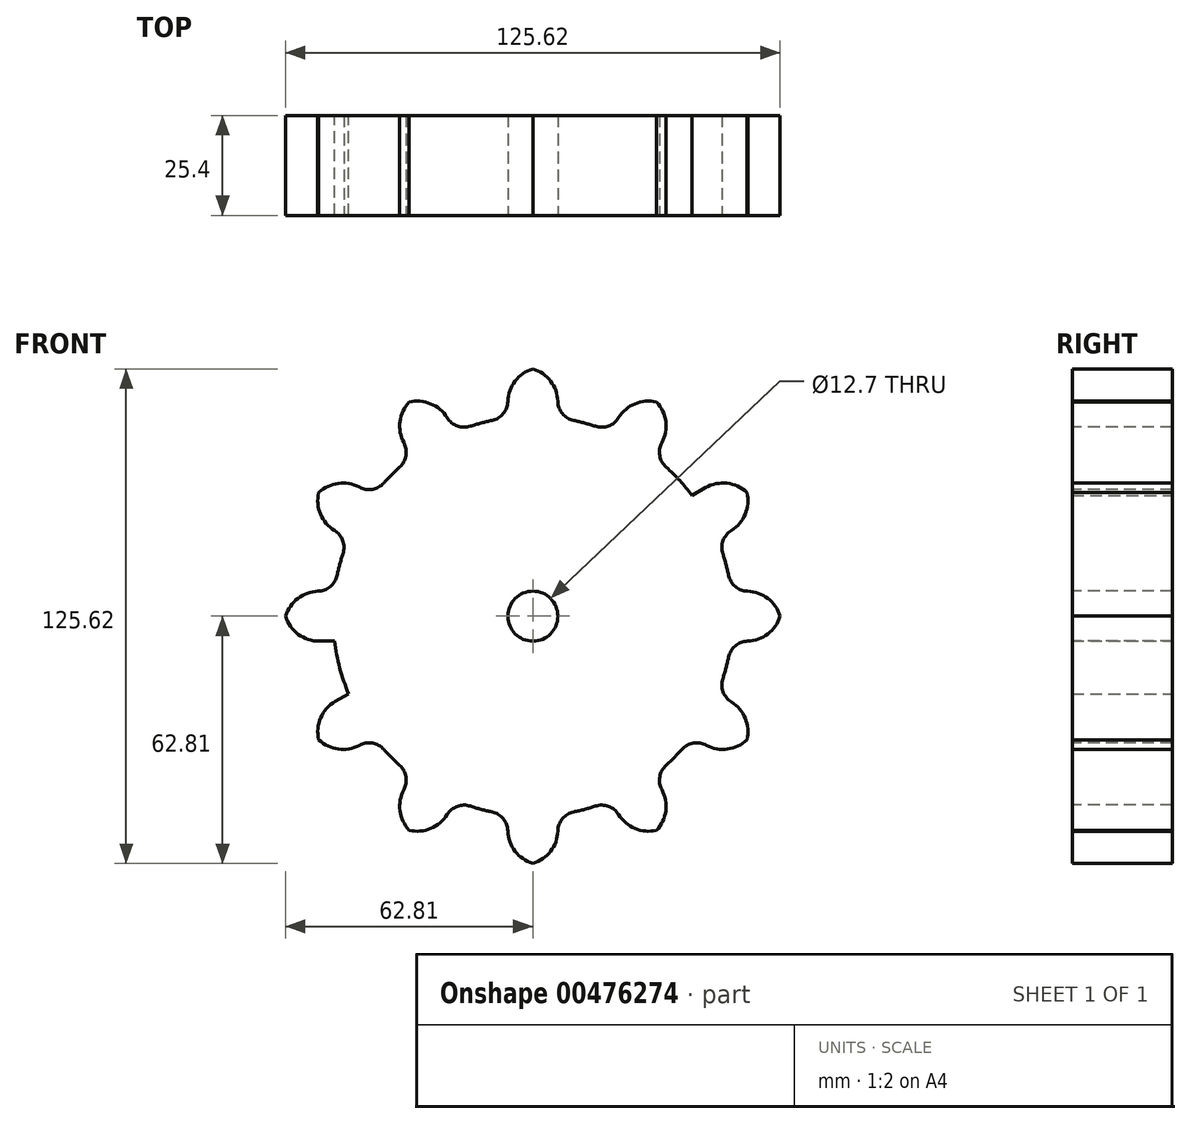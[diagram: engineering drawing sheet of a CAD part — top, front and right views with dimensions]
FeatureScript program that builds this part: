
annotation { "Feature Type Name" : "Feature", "Feature Type Description" : "" }
export const myFeature = defineFeature(function(context is Context, id is Id, definition is map)
    precondition{}
    {
        {
            var Q0;
            Q0=qCreatedBy(makeId("Front.planeOp"),FACE);
            var sketch = newSketch(context, id + "F0", { "sketchPlane" : qUnion([Q0])});
            skCircle(sketch, "E0", {"center": v(0, 0) * mm, "radius": 6.35 * mm});
            skCircle(sketch, "E1", {"center": v(0, 0) * mm, "radius": 50.8 * mm});
            skCircle(sketch, "E2", {"center": v(0, 0) * mm, "radius": 63.5 * mm, "construction": true});
            skLineSegment(sketch, "E3", {"start": v(0, 0) * mm, "end": v(0, 63.5) * mm, "construction": true});
            skLineSegment(sketch, "E4", {"start": v(0, 0) * mm, "end": v(-63.5, 0) * mm, "construction": true});
            skLineSegment(sketch, "E5", {"start": v(0, 0) * mm, "end": v(63.5, 0) * mm, "construction": true});
            skLineSegment(sketch, "E6", {"start": v(0, 0) * mm, "end": v(0, -63.5) * mm, "construction": true});
            skLineSegment(sketch, "E7", {"start": v(31.75, 55) * mm, "end": v(0, 0) * mm, "construction": true});
            skLineSegment(sketch, "E8", {"start": v(0, 0) * mm, "end": v(55, 31.75) * mm, "construction": true});
            skLineSegment(sketch, "E9.bottom", {"start": v(-6.35, -63.18) * mm, "end": v(6.35, -63.18) * mm});
            skLineSegment(sketch, "E9.top", {"start": v(-6.35, 63.18) * mm, "end": v(6.35, 63.18) * mm});
            skLineSegment(sketch, "E9.left", {"start": v(-6.35, -63.18) * mm, "end": v(-6.35, 63.18) * mm});
            skLineSegment(sketch, "E9.right", {"start": v(6.35, -63.18) * mm, "end": v(6.35, 63.18) * mm});
            skLineSegment(sketch, "E10", {"start": v(-37.1, -51.54) * mm, "end": v(26.1, 57.9) * mm});
            skLineSegment(sketch, "E11", {"start": v(-26.1, -57.9) * mm, "end": v(37.1, 51.54) * mm});
            skLineSegment(sketch, "E12", {"start": v(37.1, 51.54) * mm, "end": v(26.1, 57.9) * mm});
            skLineSegment(sketch, "E13", {"start": v(-37.1, -51.54) * mm, "end": v(-26.1, -57.9) * mm});
            skLineSegment(sketch, "E14", {"start": v(-57.9, -26.1) * mm, "end": v(51.54, 37.1) * mm});
            skLineSegment(sketch, "E15", {"start": v(51.54, 37.1) * mm, "end": v(57.9, 26.1) * mm});
            skSolve(sketch);
        }
        {
            var Q0;
            {var subQ5=sQuery(id+"F0.wireOp",EDGE,"E12");Q0=makeQuery(id+"F0.imprint","IMPRINT",FACE,{"disambiguationData":[TD([[makeQuery(id+"F0.imprint","IMPRINT",EDGE,{"derivedFrom":subQ5}),1.0]])]});}
            var Q1;
            {var subQ5=sQuery(id+"F0.wireOp",EDGE,"E9.top");Q1=makeQuery(id+"F0.imprint","IMPRINT",FACE,{"disambiguationData":[TD([[makeQuery(id+"F0.imprint","IMPRINT",EDGE,{"derivedFrom":subQ5}),-1.0]])]});}
            var Q2;
            {var subQ5=sQuery(id+"F0.wireOp",EDGE,"E13");Q2=makeQuery(id+"F0.imprint","IMPRINT",FACE,{"disambiguationData":[TD([[makeQuery(id+"F0.imprint","IMPRINT",EDGE,{"derivedFrom":subQ5}),1.0]])]});}
            var Q3;
            {var subQ5=sQuery(id+"F0.wireOp",EDGE,"E9.bottom");Q3=makeQuery(id+"F0.imprint","IMPRINT",FACE,{"disambiguationData":[TD([[makeQuery(id+"F0.imprint","IMPRINT",EDGE,{"derivedFrom":subQ5}),1.0]])]});}
            var Q4;
            {var subQ0=sQuery(id+"F0.wireOp",EDGE,"E14");var subQ1=sQuery(id+"F0.wireOp",EDGE,"E1");var subQ2=makeQuery(id+"F0.imprint","INTERSECT",VERTEX,{"disambiguationData":[OD(0.0)],"derivedFrom":[subQ1,subQ0]});Q4=makeQuery(id+"F0.imprint","IMPRINT",FACE,{"disambiguationData":[TD([[makeQuery(id+"F0.imprint","IMPRINT",EDGE,{"disambiguationData":[TD([[subQ2,-1.0]])],"derivedFrom":subQ1}),1.0]])]});}
            var Q5;
            {var subQ0=sQuery(id+"F0.wireOp",EDGE,"E10");var subQ1=sQuery(id+"F0.wireOp",EDGE,"E1");var subQ2=makeQuery(id+"F0.imprint","INTERSECT",VERTEX,{"disambiguationData":[OD(0.0)],"derivedFrom":[subQ1,subQ0]});Q5=makeQuery(id+"F0.imprint","IMPRINT",FACE,{"disambiguationData":[TD([[makeQuery(id+"F0.imprint","IMPRINT",EDGE,{"disambiguationData":[TD([[subQ2,-1.0]])],"derivedFrom":subQ1}),1.0]])]});}
            var Q6;
            {var subQ0=sQuery(id+"F0.wireOp",EDGE,"E14");var subQ1=sQuery(id+"F0.wireOp",EDGE,"E1");var subQ2=makeQuery(id+"F0.imprint","INTERSECT",VERTEX,{"disambiguationData":[OD(1.0)],"derivedFrom":[subQ1,subQ0]});Q6=makeQuery(id+"F0.imprint","IMPRINT",FACE,{"disambiguationData":[TD([[makeQuery(id+"F0.imprint","IMPRINT",EDGE,{"disambiguationData":[TD([[subQ2,1.0]])],"derivedFrom":subQ1}),1.0]])]});}
            var Q7;
            {var subQ0=sQuery(id+"F0.wireOp",EDGE,"E11");var subQ1=sQuery(id+"F0.wireOp",EDGE,"E1");var subQ2=makeQuery(id+"F0.imprint","INTERSECT",VERTEX,{"disambiguationData":[OD(1.0)],"derivedFrom":[subQ1,subQ0]});Q7=makeQuery(id+"F0.imprint","IMPRINT",FACE,{"disambiguationData":[TD([[makeQuery(id+"F0.imprint","IMPRINT",EDGE,{"disambiguationData":[TD([[subQ2,-1.0]])],"derivedFrom":subQ1}),1.0]])]});}
            var Q8;
            {var subQ0=sQuery(id+"F0.wireOp",EDGE,"E14");var subQ1=sQuery(id+"F0.wireOp",EDGE,"E1");var subQ2=makeQuery(id+"F0.imprint","INTERSECT",VERTEX,{"disambiguationData":[OD(1.0)],"derivedFrom":[subQ1,subQ0]});Q8=makeQuery(id+"F0.imprint","IMPRINT",FACE,{"disambiguationData":[TD([[makeQuery(id+"F0.imprint","IMPRINT",EDGE,{"disambiguationData":[TD([[subQ2,-1.0]])],"derivedFrom":subQ1}),1.0]])]});}
            var Q9;
            {var subQ0=sQuery(id+"F0.wireOp",EDGE,"E14");var subQ1=sQuery(id+"F0.wireOp",EDGE,"E1");var subQ2=makeQuery(id+"F0.imprint","INTERSECT",VERTEX,{"disambiguationData":[OD(0.0)],"derivedFrom":[subQ1,subQ0]});Q9=makeQuery(id+"F0.imprint","IMPRINT",FACE,{"disambiguationData":[TD([[makeQuery(id+"F0.imprint","IMPRINT",EDGE,{"disambiguationData":[TD([[subQ2,1.0]])],"derivedFrom":subQ1}),1.0]])]});}
            var Q10;
            {var subQ0=sQuery(id+"F0.wireOp",EDGE,"E11");var subQ1=sQuery(id+"F0.wireOp",EDGE,"E1");var subQ2=makeQuery(id+"F0.imprint","INTERSECT",VERTEX,{"disambiguationData":[OD(0.0)],"derivedFrom":[subQ1,subQ0]});Q10=makeQuery(id+"F0.imprint","IMPRINT",FACE,{"disambiguationData":[TD([[makeQuery(id+"F0.imprint","IMPRINT",EDGE,{"disambiguationData":[TD([[subQ2,-1.0]])],"derivedFrom":subQ1}),1.0]])]});}
            var Q11;
            {var subQ1=sQuery(id+"F0.wireOp",EDGE,"E9.right");var subQ5=sQuery(id+"F0.wireOp",EDGE,"E1");var subQ6=makeQuery(id+"F0.imprint","INTERSECT",VERTEX,{"disambiguationData":[OD(0.0)],"derivedFrom":[subQ5,subQ1]});Q11=makeQuery(id+"F0.imprint","IMPRINT",FACE,{"disambiguationData":[TD([[makeQuery(id+"F0.imprint","IMPRINT",EDGE,{"disambiguationData":[TD([[subQ6,-1.0]])],"derivedFrom":subQ5}),1.0]])]});}
            var Q12;
            {var subQ0=sQuery(id+"F0.wireOp",EDGE,"E10");var subQ1=sQuery(id+"F0.wireOp",EDGE,"E1");var subQ2=makeQuery(id+"F0.imprint","INTERSECT",VERTEX,{"disambiguationData":[OD(1.0)],"derivedFrom":[subQ1,subQ0]});Q12=makeQuery(id+"F0.imprint","IMPRINT",FACE,{"disambiguationData":[TD([[makeQuery(id+"F0.imprint","IMPRINT",EDGE,{"disambiguationData":[TD([[subQ2,-1.0]])],"derivedFrom":subQ1}),1.0]])]});}
            var Q13;
            {var subQ2=sQuery(id+"F0.wireOp",EDGE,"E9.left");var subQ4=sQuery(id+"F0.wireOp",EDGE,"E1");var subQ5=makeQuery(id+"F0.imprint","INTERSECT",VERTEX,{"disambiguationData":[OD(1.0)],"derivedFrom":[subQ4,subQ2]});Q13=makeQuery(id+"F0.imprint","IMPRINT",FACE,{"disambiguationData":[TD([[makeQuery(id+"F0.imprint","IMPRINT",EDGE,{"disambiguationData":[TD([[subQ5,-1.0]])],"derivedFrom":subQ4}),1.0]])]});}
            var Q14;
            {var subQ0=sQuery(id+"F0.wireOp",EDGE,"E14");var subQ1=sQuery(id+"F0.wireOp",EDGE,"E9.right");var subQ2=makeQuery(id+"F0.imprint","INTERSECT",VERTEX,{"derivedFrom":[subQ1,subQ0]});Q14=makeQuery(id+"F0.imprint","IMPRINT",FACE,{"disambiguationData":[TD([[makeQuery(id+"F0.imprint","IMPRINT",EDGE,{"disambiguationData":[TD([[subQ2,-1.0]])],"derivedFrom":subQ1}),1.0]])]});}
            var Q15;
            {var subQ0=sQuery(id+"F0.wireOp",EDGE,"E0");var subQ4=makeQuery(id+"F0.imprint","INTERSECT",VERTEX,{"derivedFrom":[subQ0,sQuery(id+"F0.wireOp",EDGE,"E14")]});Q15=makeQuery(id+"F0.imprint","IMPRINT",FACE,{"disambiguationData":[TD([[makeQuery(id+"F0.imprint","IMPRINT",EDGE,{"disambiguationData":[TD([[subQ4,1.0]])],"derivedFrom":subQ0}),1.0]])]});}
            var Q16;
            {var subQ0=sQuery(id+"F0.wireOp",EDGE,"E9.right");var subQ1=makeQuery(id+"F0.imprint","INTERSECT",VERTEX,{"derivedFrom":[sQuery(id+"F0.wireOp",EDGE,"E0"),subQ0]});Q16=makeQuery(id+"F0.imprint","IMPRINT",FACE,{"disambiguationData":[TD([[makeQuery(id+"F0.imprint","IMPRINT",EDGE,{"disambiguationData":[TD([[subQ1,1.0]])],"derivedFrom":subQ0}),-1.0]])]});}
            var Q17;
            {var subQ0=sQuery(id+"F0.wireOp",EDGE,"E14");var subQ1=sQuery(id+"F0.wireOp",EDGE,"E0");var subQ2=makeQuery(id+"F0.imprint","INTERSECT",VERTEX,{"derivedFrom":[subQ1,subQ0]});Q17=makeQuery(id+"F0.imprint","IMPRINT",FACE,{"disambiguationData":[TD([[makeQuery(id+"F0.imprint","IMPRINT",EDGE,{"disambiguationData":[TD([[subQ2,1.0]])],"derivedFrom":subQ1}),-1.0]])]});}
            var Q18;
            {var subQ0=sQuery(id+"F0.wireOp",EDGE,"E9.left");var subQ1=sQuery(id+"F0.wireOp",EDGE,"E0");var subQ2=makeQuery(id+"F0.imprint","INTERSECT",VERTEX,{"derivedFrom":[subQ1,subQ0]});Q18=makeQuery(id+"F0.imprint","IMPRINT",FACE,{"disambiguationData":[TD([[makeQuery(id+"F0.imprint","IMPRINT",EDGE,{"disambiguationData":[TD([[subQ2,-1.0]])],"derivedFrom":subQ1}),-1.0]])]});}
            var Q19;
            {var subQ0=sQuery(id+"F0.wireOp",EDGE,"E10");var subQ1=sQuery(id+"F0.wireOp",EDGE,"E9.left");var subQ2=makeQuery(id+"F0.imprint","INTERSECT",VERTEX,{"derivedFrom":[subQ1,subQ0]});Q19=makeQuery(id+"F0.imprint","IMPRINT",FACE,{"disambiguationData":[TD([[makeQuery(id+"F0.imprint","IMPRINT",EDGE,{"disambiguationData":[TD([[subQ2,-1.0]])],"derivedFrom":subQ1}),-1.0]])]});}
            var Q20;
            {var subQ0=sQuery(id+"F0.wireOp",EDGE,"E9.right");var subQ1=sQuery(id+"F0.wireOp",EDGE,"E0");var subQ2=makeQuery(id+"F0.imprint","INTERSECT",VERTEX,{"derivedFrom":[subQ1,subQ0]});Q20=makeQuery(id+"F0.imprint","IMPRINT",FACE,{"disambiguationData":[TD([[makeQuery(id+"F0.imprint","IMPRINT",EDGE,{"disambiguationData":[TD([[subQ2,1.0]])],"derivedFrom":subQ1}),-1.0]])]});}
            var Q21;
            {var subQ0=sQuery(id+"F0.wireOp",EDGE,"E14");var subQ1=sQuery(id+"F0.wireOp",EDGE,"E0");var subQ2=makeQuery(id+"F0.imprint","INTERSECT",VERTEX,{"derivedFrom":[subQ1,subQ0]});Q21=makeQuery(id+"F0.imprint","IMPRINT",FACE,{"disambiguationData":[TD([[makeQuery(id+"F0.imprint","IMPRINT",EDGE,{"disambiguationData":[TD([[subQ2,-1.0]])],"derivedFrom":subQ1}),-1.0]])]});}
            var Q22;
            {var subQ0=sQuery(id+"F0.wireOp",EDGE,"E10");var subQ1=sQuery(id+"F0.wireOp",EDGE,"E0");var subQ2=makeQuery(id+"F0.imprint","INTERSECT",VERTEX,{"derivedFrom":[subQ1,subQ0]});Q22=makeQuery(id+"F0.imprint","IMPRINT",FACE,{"disambiguationData":[TD([[makeQuery(id+"F0.imprint","IMPRINT",EDGE,{"disambiguationData":[TD([[subQ2,-1.0]])],"derivedFrom":subQ1}),-1.0]])]});}
            extrude(context, id + "F1", {"entities" : qUnion([Q0, Q1, Q2, Q3, Q4, Q5, Q6, Q7, Q8, Q9, Q10, Q11, Q12, Q13, Q14, Q15, Q16, Q17, Q18, Q19, Q20, Q21, Q22]), "depth" : 25.4 * mm});
        }
        {
            var Q0;
            Q0=qCreatedBy(makeId("Front.planeOp"),FACE);
            var sketch = newSketch(context, id + "F2", { "sketchPlane" : qUnion([Q0])});
            skCircle(sketch, "E16", {"center": v(0, 0) * mm, "radius": 6.35 * mm});
            skCircle(sketch, "E17", {"center": v(0, 0) * mm, "radius": 50.8 * mm});
            skCircle(sketch, "E18", {"center": v(0, 0) * mm, "radius": 63.5 * mm, "construction": true});
            skLineSegment(sketch, "E19", {"start": v(0, 0) * mm, "end": v(63.5, 0) * mm, "construction": true});
            skLineSegment(sketch, "E20", {"start": v(0, 0) * mm, "end": v(0, 63.5) * mm, "construction": true});
            skLineSegment(sketch, "E21", {"start": v(0, 0) * mm, "end": v(55, 31.75) * mm, "construction": true});
            skLineSegment(sketch, "E22", {"start": v(-57.9, -26.1) * mm, "end": v(51.54, 37.1) * mm});
            skLineSegment(sketch, "E23", {"start": v(51.54, 37.1) * mm, "end": v(57.9, 26.1) * mm});
            skLineSegment(sketch, "E24", {"start": v(57.9, 26.1) * mm, "end": v(-51.54, -37.1) * mm});
            skLineSegment(sketch, "E25", {"start": v(-51.54, -37.1) * mm, "end": v(-57.9, -26.1) * mm});
            skLineSegment(sketch, "E26.bottom", {"start": v(-63.18, 6.35) * mm, "end": v(63.18, 6.35) * mm});
            skLineSegment(sketch, "E26.top", {"start": v(-63.18, -6.35) * mm, "end": v(63.18, -6.35) * mm});
            skLineSegment(sketch, "E26.left", {"start": v(-63.18, 6.35) * mm, "end": v(-63.18, -6.35) * mm});
            skLineSegment(sketch, "E26.right", {"start": v(63.18, 6.35) * mm, "end": v(63.18, -6.35) * mm});
            skLineSegment(sketch, "E27", {"start": v(-57.9, 26.1) * mm, "end": v(51.54, -37.1) * mm});
            skLineSegment(sketch, "E28", {"start": v(51.54, -37.1) * mm, "end": v(57.9, -26.1) * mm});
            skLineSegment(sketch, "E29", {"start": v(57.9, -26.1) * mm, "end": v(-51.54, 37.1) * mm});
            skLineSegment(sketch, "E30", {"start": v(-51.54, 37.1) * mm, "end": v(-57.9, 26.1) * mm});
            skLineSegment(sketch, "E31", {"start": v(-37.1, 51.54) * mm, "end": v(26.1, -57.9) * mm});
            skLineSegment(sketch, "E32", {"start": v(26.1, -57.9) * mm, "end": v(37.1, -51.54) * mm});
            skLineSegment(sketch, "E33", {"start": v(37.1, -51.54) * mm, "end": v(-26.1, 57.9) * mm});
            skLineSegment(sketch, "E34", {"start": v(-26.1, 57.9) * mm, "end": v(-37.1, 51.54) * mm});
            skSolve(sketch);
        }
        {
            var Q0;
            {var subQ5=sQuery(id+"F2.wireOp",EDGE,"E23");Q0=makeQuery(id+"F2.imprint","IMPRINT",FACE,{"disambiguationData":[TD([[makeQuery(id+"F2.imprint","IMPRINT",EDGE,{"derivedFrom":subQ5}),-1.0]])]});}
            var Q1;
            {var subQ5=sQuery(id+"F2.wireOp",EDGE,"E34");Q1=makeQuery(id+"F2.imprint","IMPRINT",FACE,{"disambiguationData":[TD([[makeQuery(id+"F2.imprint","IMPRINT",EDGE,{"derivedFrom":subQ5}),1.0]])]});}
            var Q2;
            {var subQ5=sQuery(id+"F2.wireOp",EDGE,"E30");Q2=makeQuery(id+"F2.imprint","IMPRINT",FACE,{"disambiguationData":[TD([[makeQuery(id+"F2.imprint","IMPRINT",EDGE,{"derivedFrom":subQ5}),1.0]])]});}
            var Q3;
            {var subQ5=sQuery(id+"F2.wireOp",EDGE,"E26.left");Q3=makeQuery(id+"F2.imprint","IMPRINT",FACE,{"disambiguationData":[TD([[makeQuery(id+"F2.imprint","IMPRINT",EDGE,{"derivedFrom":subQ5}),1.0]])]});}
            var Q4;
            {var subQ5=sQuery(id+"F2.wireOp",EDGE,"E25");Q4=makeQuery(id+"F2.imprint","IMPRINT",FACE,{"disambiguationData":[TD([[makeQuery(id+"F2.imprint","IMPRINT",EDGE,{"derivedFrom":subQ5}),-1.0]])]});}
            var Q5;
            {var subQ5=sQuery(id+"F2.wireOp",EDGE,"E32");Q5=makeQuery(id+"F2.imprint","IMPRINT",FACE,{"disambiguationData":[TD([[makeQuery(id+"F2.imprint","IMPRINT",EDGE,{"derivedFrom":subQ5}),1.0]])]});}
            var Q6;
            {var subQ5=sQuery(id+"F2.wireOp",EDGE,"E28");Q6=makeQuery(id+"F2.imprint","IMPRINT",FACE,{"disambiguationData":[TD([[makeQuery(id+"F2.imprint","IMPRINT",EDGE,{"derivedFrom":subQ5}),1.0]])]});}
            var Q7;
            {var subQ5=sQuery(id+"F2.wireOp",EDGE,"E26.right");Q7=makeQuery(id+"F2.imprint","IMPRINT",FACE,{"disambiguationData":[TD([[makeQuery(id+"F2.imprint","IMPRINT",EDGE,{"derivedFrom":subQ5}),-1.0]])]});}
            var Q8;
            {var subQ0=sQuery(id+"F2.wireOp",EDGE,"E24");var subQ1=sQuery(id+"F2.wireOp",EDGE,"E17");var subQ2=makeQuery(id+"F2.imprint","INTERSECT",VERTEX,{"disambiguationData":[OD(0.0)],"derivedFrom":[subQ1,subQ0]});Q8=makeQuery(id+"F2.imprint","IMPRINT",FACE,{"disambiguationData":[TD([[makeQuery(id+"F2.imprint","IMPRINT",EDGE,{"disambiguationData":[TD([[subQ2,1.0]])],"derivedFrom":subQ1}),1.0]])]});}
            var Q9;
            {var subQ0=sQuery(id+"F2.wireOp",EDGE,"E22");var subQ1=sQuery(id+"F2.wireOp",EDGE,"E17");var subQ2=makeQuery(id+"F2.imprint","INTERSECT",VERTEX,{"disambiguationData":[OD(0.0)],"derivedFrom":[subQ1,subQ0]});Q9=makeQuery(id+"F2.imprint","IMPRINT",FACE,{"disambiguationData":[TD([[makeQuery(id+"F2.imprint","IMPRINT",EDGE,{"disambiguationData":[TD([[subQ2,-1.0]])],"derivedFrom":subQ1}),1.0]])]});}
            var Q10;
            {var subQ0=sQuery(id+"F2.wireOp",EDGE,"E31");var subQ1=sQuery(id+"F2.wireOp",EDGE,"E17");var subQ2=makeQuery(id+"F2.imprint","INTERSECT",VERTEX,{"disambiguationData":[OD(0.0)],"derivedFrom":[subQ1,subQ0]});Q10=makeQuery(id+"F2.imprint","IMPRINT",FACE,{"disambiguationData":[TD([[makeQuery(id+"F2.imprint","IMPRINT",EDGE,{"disambiguationData":[TD([[subQ2,-1.0]])],"derivedFrom":subQ1}),1.0]])]});}
            var Q11;
            {var subQ0=sQuery(id+"F2.wireOp",EDGE,"E27");var subQ1=sQuery(id+"F2.wireOp",EDGE,"E17");var subQ2=makeQuery(id+"F2.imprint","INTERSECT",VERTEX,{"disambiguationData":[OD(0.0)],"derivedFrom":[subQ1,subQ0]});Q11=makeQuery(id+"F2.imprint","IMPRINT",FACE,{"disambiguationData":[TD([[makeQuery(id+"F2.imprint","IMPRINT",EDGE,{"disambiguationData":[TD([[subQ2,-1.0]])],"derivedFrom":subQ1}),1.0]])]});}
            var Q12;
            {var subQ0=sQuery(id+"F2.wireOp",EDGE,"E26.top");var subQ1=sQuery(id+"F2.wireOp",EDGE,"E17");var subQ2=makeQuery(id+"F2.imprint","INTERSECT",VERTEX,{"disambiguationData":[OD(0.0)],"derivedFrom":[subQ1,subQ0]});Q12=makeQuery(id+"F2.imprint","IMPRINT",FACE,{"disambiguationData":[TD([[makeQuery(id+"F2.imprint","IMPRINT",EDGE,{"disambiguationData":[TD([[subQ2,-1.0]])],"derivedFrom":subQ1}),1.0]])]});}
            var Q13;
            {var subQ0=sQuery(id+"F2.wireOp",EDGE,"E24");var subQ1=sQuery(id+"F2.wireOp",EDGE,"E17");var subQ2=makeQuery(id+"F2.imprint","INTERSECT",VERTEX,{"disambiguationData":[OD(1.0)],"derivedFrom":[subQ1,subQ0]});Q13=makeQuery(id+"F2.imprint","IMPRINT",FACE,{"disambiguationData":[TD([[makeQuery(id+"F2.imprint","IMPRINT",EDGE,{"disambiguationData":[TD([[subQ2,-1.0]])],"derivedFrom":subQ1}),1.0]])]});}
            var Q14;
            {var subQ0=sQuery(id+"F2.wireOp",EDGE,"E33");var subQ1=sQuery(id+"F2.wireOp",EDGE,"E17");var subQ2=makeQuery(id+"F2.imprint","INTERSECT",VERTEX,{"disambiguationData":[OD(1.0)],"derivedFrom":[subQ1,subQ0]});Q14=makeQuery(id+"F2.imprint","IMPRINT",FACE,{"disambiguationData":[TD([[makeQuery(id+"F2.imprint","IMPRINT",EDGE,{"disambiguationData":[TD([[subQ2,-1.0]])],"derivedFrom":subQ1}),1.0]])]});}
            var Q15;
            {var subQ0=sQuery(id+"F2.wireOp",EDGE,"E29");var subQ1=sQuery(id+"F2.wireOp",EDGE,"E17");var subQ2=makeQuery(id+"F2.imprint","INTERSECT",VERTEX,{"disambiguationData":[OD(1.0)],"derivedFrom":[subQ1,subQ0]});Q15=makeQuery(id+"F2.imprint","IMPRINT",FACE,{"disambiguationData":[TD([[makeQuery(id+"F2.imprint","IMPRINT",EDGE,{"disambiguationData":[TD([[subQ2,-1.0]])],"derivedFrom":subQ1}),1.0]])]});}
            var Q16;
            {var subQ1=sQuery(id+"F2.wireOp",EDGE,"E24");var subQ5=sQuery(id+"F2.wireOp",EDGE,"E17");var subQ6=makeQuery(id+"F2.imprint","INTERSECT",VERTEX,{"disambiguationData":[OD(0.0)],"derivedFrom":[subQ5,subQ1]});Q16=makeQuery(id+"F2.imprint","IMPRINT",FACE,{"disambiguationData":[TD([[makeQuery(id+"F2.imprint","IMPRINT",EDGE,{"disambiguationData":[TD([[subQ6,-1.0]])],"derivedFrom":subQ5}),1.0]])]});}
            var Q17;
            {var subQ1=sQuery(id+"F2.wireOp",EDGE,"E17");var subQ7=sQuery(id+"F2.wireOp",EDGE,"E33");var subQ9=makeQuery(id+"F2.imprint","INTERSECT",VERTEX,{"disambiguationData":[OD(0.0)],"derivedFrom":[subQ1,subQ7]});Q17=makeQuery(id+"F2.imprint","IMPRINT",FACE,{"disambiguationData":[TD([[makeQuery(id+"F2.imprint","IMPRINT",EDGE,{"disambiguationData":[TD([[subQ9,-1.0]])],"derivedFrom":subQ1}),1.0]])]});}
            var Q18;
            {var subQ0=sQuery(id+"F2.wireOp",EDGE,"E29");var subQ1=sQuery(id+"F2.wireOp",EDGE,"E17");var subQ2=makeQuery(id+"F2.imprint","INTERSECT",VERTEX,{"disambiguationData":[OD(0.0)],"derivedFrom":[subQ1,subQ0]});Q18=makeQuery(id+"F2.imprint","IMPRINT",FACE,{"disambiguationData":[TD([[makeQuery(id+"F2.imprint","IMPRINT",EDGE,{"disambiguationData":[TD([[subQ2,-1.0]])],"derivedFrom":subQ1}),1.0]])]});}
            var Q19;
            {var subQ1=sQuery(id+"F2.wireOp",EDGE,"E17");var subQ5=sQuery(id+"F2.wireOp",EDGE,"E26.bottom");var subQ6=makeQuery(id+"F2.imprint","INTERSECT",VERTEX,{"disambiguationData":[OD(1.0)],"derivedFrom":[subQ1,subQ5]});Q19=makeQuery(id+"F2.imprint","IMPRINT",FACE,{"disambiguationData":[TD([[makeQuery(id+"F2.imprint","IMPRINT",EDGE,{"disambiguationData":[TD([[subQ6,-1.0]])],"derivedFrom":subQ1}),1.0]])]});}
            var Q20;
            {var subQ1=sQuery(id+"F2.wireOp",EDGE,"E22");var subQ5=sQuery(id+"F2.wireOp",EDGE,"E17");var subQ6=makeQuery(id+"F2.imprint","INTERSECT",VERTEX,{"disambiguationData":[OD(1.0)],"derivedFrom":[subQ5,subQ1]});Q20=makeQuery(id+"F2.imprint","IMPRINT",FACE,{"disambiguationData":[TD([[makeQuery(id+"F2.imprint","IMPRINT",EDGE,{"disambiguationData":[TD([[subQ6,-1.0]])],"derivedFrom":subQ5}),1.0]])]});}
            var Q21;
            {var subQ0=sQuery(id+"F2.wireOp",EDGE,"E31");var subQ1=sQuery(id+"F2.wireOp",EDGE,"E17");var subQ2=makeQuery(id+"F2.imprint","INTERSECT",VERTEX,{"disambiguationData":[OD(1.0)],"derivedFrom":[subQ1,subQ0]});Q21=makeQuery(id+"F2.imprint","IMPRINT",FACE,{"disambiguationData":[TD([[makeQuery(id+"F2.imprint","IMPRINT",EDGE,{"disambiguationData":[TD([[subQ2,-1.0]])],"derivedFrom":subQ1}),1.0]])]});}
            var Q22;
            {var subQ1=sQuery(id+"F2.wireOp",EDGE,"E17");var subQ7=sQuery(id+"F2.wireOp",EDGE,"E27");var subQ8=makeQuery(id+"F2.imprint","INTERSECT",VERTEX,{"disambiguationData":[OD(1.0)],"derivedFrom":[subQ1,subQ7]});Q22=makeQuery(id+"F2.imprint","IMPRINT",FACE,{"disambiguationData":[TD([[makeQuery(id+"F2.imprint","IMPRINT",EDGE,{"disambiguationData":[TD([[subQ8,-1.0]])],"derivedFrom":subQ1}),1.0]])]});}
            var Q23;
            {var subQ1=sQuery(id+"F2.wireOp",EDGE,"E17");var subQ5=sQuery(id+"F2.wireOp",EDGE,"E26.bottom");var subQ6=makeQuery(id+"F2.imprint","INTERSECT",VERTEX,{"disambiguationData":[OD(0.0)],"derivedFrom":[subQ1,subQ5]});Q23=makeQuery(id+"F2.imprint","IMPRINT",FACE,{"disambiguationData":[TD([[makeQuery(id+"F2.imprint","IMPRINT",EDGE,{"disambiguationData":[TD([[subQ6,1.0]])],"derivedFrom":subQ1}),1.0]])]});}
            var Q24;
            {var subQ0=sQuery(id+"F2.wireOp",EDGE,"E27");var subQ1=sQuery(id+"F2.wireOp",EDGE,"E22");var subQ2=makeQuery(id+"F2.imprint","INTERSECT",VERTEX,{"derivedFrom":[subQ1,subQ0]});Q24=makeQuery(id+"F2.imprint","IMPRINT",FACE,{"disambiguationData":[TD([[makeQuery(id+"F2.imprint","IMPRINT",EDGE,{"disambiguationData":[TD([[subQ2,-1.0]])],"derivedFrom":subQ1}),1.0]])]});}
            var Q25;
            {var subQ0=sQuery(id+"F2.wireOp",EDGE,"E22");var subQ1=sQuery(id+"F2.wireOp",EDGE,"E16");var subQ2=makeQuery(id+"F2.imprint","INTERSECT",VERTEX,{"derivedFrom":[subQ1,subQ0]});Q25=makeQuery(id+"F2.imprint","IMPRINT",FACE,{"disambiguationData":[TD([[makeQuery(id+"F2.imprint","IMPRINT",EDGE,{"disambiguationData":[TD([[subQ2,-1.0]])],"derivedFrom":subQ1}),-1.0]])]});}
            var Q26;
            {var subQ0=sQuery(id+"F2.wireOp",EDGE,"E26.bottom");var subQ1=sQuery(id+"F2.wireOp",EDGE,"E24");var subQ2=makeQuery(id+"F2.imprint","INTERSECT",VERTEX,{"derivedFrom":[subQ1,subQ0]});Q26=makeQuery(id+"F2.imprint","IMPRINT",FACE,{"disambiguationData":[TD([[makeQuery(id+"F2.imprint","IMPRINT",EDGE,{"disambiguationData":[TD([[subQ2,-1.0]])],"derivedFrom":subQ1}),-1.0]])]});}
            var Q27;
            {var subQ0=sQuery(id+"F2.wireOp",EDGE,"E24");var subQ1=makeQuery(id+"F2.imprint","INTERSECT",VERTEX,{"derivedFrom":[sQuery(id+"F2.wireOp",EDGE,"E16"),subQ0]});Q27=makeQuery(id+"F2.imprint","IMPRINT",FACE,{"disambiguationData":[TD([[makeQuery(id+"F2.imprint","IMPRINT",EDGE,{"disambiguationData":[TD([[subQ1,1.0]])],"derivedFrom":subQ0}),1.0]])]});}
            var Q28;
            {var subQ0=sQuery(id+"F2.wireOp",EDGE,"E26.top");var subQ1=sQuery(id+"F2.wireOp",EDGE,"E22");var subQ2=makeQuery(id+"F2.imprint","INTERSECT",VERTEX,{"derivedFrom":[subQ1,subQ0]});Q28=makeQuery(id+"F2.imprint","IMPRINT",FACE,{"disambiguationData":[TD([[makeQuery(id+"F2.imprint","IMPRINT",EDGE,{"disambiguationData":[TD([[subQ2,-1.0]])],"derivedFrom":subQ1}),-1.0]])]});}
            var Q29;
            {var subQ0=sQuery(id+"F2.wireOp",EDGE,"E26.bottom");var subQ1=sQuery(id+"F2.wireOp",EDGE,"E22");var subQ2=makeQuery(id+"F2.imprint","INTERSECT",VERTEX,{"derivedFrom":[subQ1,subQ0]});Q29=makeQuery(id+"F2.imprint","IMPRINT",FACE,{"disambiguationData":[TD([[makeQuery(id+"F2.imprint","IMPRINT",EDGE,{"disambiguationData":[TD([[subQ2,-1.0]])],"derivedFrom":subQ1}),1.0]])]});}
            var Q30;
            {var subQ0=sQuery(id+"F2.wireOp",EDGE,"E27");var subQ1=sQuery(id+"F2.wireOp",EDGE,"E22");var subQ2=makeQuery(id+"F2.imprint","INTERSECT",VERTEX,{"derivedFrom":[subQ1,subQ0]});Q30=makeQuery(id+"F2.imprint","IMPRINT",FACE,{"disambiguationData":[TD([[makeQuery(id+"F2.imprint","IMPRINT",EDGE,{"disambiguationData":[TD([[subQ2,-1.0]])],"derivedFrom":subQ1}),-1.0]])]});}
            var Q31;
            {var subQ0=sQuery(id+"F2.wireOp",EDGE,"E26.top");var subQ1=sQuery(id+"F2.wireOp",EDGE,"E24");var subQ2=makeQuery(id+"F2.imprint","INTERSECT",VERTEX,{"derivedFrom":[subQ1,subQ0]});Q31=makeQuery(id+"F2.imprint","IMPRINT",FACE,{"disambiguationData":[TD([[makeQuery(id+"F2.imprint","IMPRINT",EDGE,{"disambiguationData":[TD([[subQ2,-1.0]])],"derivedFrom":subQ1}),1.0]])]});}
            var Q32;
            {var subQ0=sQuery(id+"F2.wireOp",EDGE,"E29");var subQ1=sQuery(id+"F2.wireOp",EDGE,"E24");var subQ2=makeQuery(id+"F2.imprint","INTERSECT",VERTEX,{"derivedFrom":[subQ1,subQ0]});Q32=makeQuery(id+"F2.imprint","IMPRINT",FACE,{"disambiguationData":[TD([[makeQuery(id+"F2.imprint","IMPRINT",EDGE,{"disambiguationData":[TD([[subQ2,-1.0]])],"derivedFrom":subQ1}),-1.0]])]});}
            var Q33;
            {var subQ0=sQuery(id+"F2.wireOp",EDGE,"E27");var subQ1=sQuery(id+"F2.wireOp",EDGE,"E24");var subQ2=makeQuery(id+"F2.imprint","INTERSECT",VERTEX,{"derivedFrom":[subQ1,subQ0]});Q33=makeQuery(id+"F2.imprint","IMPRINT",FACE,{"disambiguationData":[TD([[makeQuery(id+"F2.imprint","IMPRINT",EDGE,{"disambiguationData":[TD([[subQ2,-1.0]])],"derivedFrom":subQ1}),-1.0]])]});}
            var Q34;
            {var subQ0=sQuery(id+"F2.wireOp",EDGE,"E33");var subQ1=sQuery(id+"F2.wireOp",EDGE,"E16");var subQ2=makeQuery(id+"F2.imprint","INTERSECT",VERTEX,{"derivedFrom":[subQ1,subQ0]});Q34=makeQuery(id+"F2.imprint","IMPRINT",FACE,{"disambiguationData":[TD([[makeQuery(id+"F2.imprint","IMPRINT",EDGE,{"disambiguationData":[TD([[subQ2,1.0]])],"derivedFrom":subQ1}),-1.0]])]});}
            var Q35;
            {var subQ0=sQuery(id+"F2.wireOp",EDGE,"E22");var subQ1=makeQuery(id+"F2.imprint","INTERSECT",VERTEX,{"derivedFrom":[sQuery(id+"F2.wireOp",EDGE,"E16"),subQ0]});Q35=makeQuery(id+"F2.imprint","IMPRINT",FACE,{"disambiguationData":[TD([[makeQuery(id+"F2.imprint","IMPRINT",EDGE,{"disambiguationData":[TD([[subQ1,1.0]])],"derivedFrom":subQ0}),1.0]])]});}
            var Q36;
            {var subQ0=sQuery(id+"F2.wireOp",EDGE,"E29");var subQ1=sQuery(id+"F2.wireOp",EDGE,"E24");var subQ2=makeQuery(id+"F2.imprint","INTERSECT",VERTEX,{"derivedFrom":[subQ1,subQ0]});Q36=makeQuery(id+"F2.imprint","IMPRINT",FACE,{"disambiguationData":[TD([[makeQuery(id+"F2.imprint","IMPRINT",EDGE,{"disambiguationData":[TD([[subQ2,-1.0]])],"derivedFrom":subQ1}),1.0]])]});}
            var Q37;
            {var subQ0=sQuery(id+"F2.wireOp",EDGE,"E26.top");var subQ1=sQuery(id+"F2.wireOp",EDGE,"E24");var subQ2=makeQuery(id+"F2.imprint","INTERSECT",VERTEX,{"derivedFrom":[subQ1,subQ0]});Q37=makeQuery(id+"F2.imprint","IMPRINT",FACE,{"disambiguationData":[TD([[makeQuery(id+"F2.imprint","IMPRINT",EDGE,{"disambiguationData":[TD([[subQ2,-1.0]])],"derivedFrom":subQ1}),-1.0]])]});}
            var Q38;
            {var subQ0=sQuery(id+"F2.wireOp",EDGE,"E29");var subQ1=sQuery(id+"F2.wireOp",EDGE,"E26.bottom");var subQ2=makeQuery(id+"F2.imprint","INTERSECT",VERTEX,{"derivedFrom":[subQ1,subQ0]});Q38=makeQuery(id+"F2.imprint","IMPRINT",FACE,{"disambiguationData":[TD([[makeQuery(id+"F2.imprint","IMPRINT",EDGE,{"disambiguationData":[TD([[subQ2,-1.0]])],"derivedFrom":subQ1}),-1.0]])]});}
            var Q39;
            {var subQ0=sQuery(id+"F2.wireOp",EDGE,"E29");var subQ1=sQuery(id+"F2.wireOp",EDGE,"E22");var subQ2=makeQuery(id+"F2.imprint","INTERSECT",VERTEX,{"derivedFrom":[subQ1,subQ0]});Q39=makeQuery(id+"F2.imprint","IMPRINT",FACE,{"disambiguationData":[TD([[makeQuery(id+"F2.imprint","IMPRINT",EDGE,{"disambiguationData":[TD([[subQ2,-1.0]])],"derivedFrom":subQ1}),-1.0]])]});}
            var Q40;
            {var subQ0=sQuery(id+"F2.wireOp",EDGE,"E31");var subQ1=sQuery(id+"F2.wireOp",EDGE,"E26.top");var subQ2=makeQuery(id+"F2.imprint","INTERSECT",VERTEX,{"derivedFrom":[subQ1,subQ0]});Q40=makeQuery(id+"F2.imprint","IMPRINT",FACE,{"disambiguationData":[TD([[makeQuery(id+"F2.imprint","IMPRINT",EDGE,{"disambiguationData":[TD([[subQ2,-1.0]])],"derivedFrom":subQ1}),1.0]])]});}
            var Q41;
            {var subQ0=sQuery(id+"F2.wireOp",EDGE,"E16");var subQ4=makeQuery(id+"F2.imprint","INTERSECT",VERTEX,{"derivedFrom":[subQ0,sQuery(id+"F2.wireOp",EDGE,"E29")]});Q41=makeQuery(id+"F2.imprint","IMPRINT",FACE,{"disambiguationData":[TD([[makeQuery(id+"F2.imprint","IMPRINT",EDGE,{"disambiguationData":[TD([[subQ4,1.0]])],"derivedFrom":subQ0}),1.0]])]});}
            var Q42;
            {var subQ0=sQuery(id+"F2.wireOp",EDGE,"E26.bottom");var subQ1=sQuery(id+"F2.wireOp",EDGE,"E16");var subQ2=makeQuery(id+"F2.imprint","INTERSECT",VERTEX,{"derivedFrom":[subQ1,subQ0]});Q42=makeQuery(id+"F2.imprint","IMPRINT",FACE,{"disambiguationData":[TD([[makeQuery(id+"F2.imprint","IMPRINT",EDGE,{"disambiguationData":[TD([[subQ2,-1.0]])],"derivedFrom":subQ1}),-1.0]])]});}
            var Q43;
            {var subQ0=sQuery(id+"F2.wireOp",EDGE,"E26.top");var subQ1=sQuery(id+"F2.wireOp",EDGE,"E16");var subQ2=makeQuery(id+"F2.imprint","INTERSECT",VERTEX,{"derivedFrom":[subQ1,subQ0]});Q43=makeQuery(id+"F2.imprint","IMPRINT",FACE,{"disambiguationData":[TD([[makeQuery(id+"F2.imprint","IMPRINT",EDGE,{"disambiguationData":[TD([[subQ2,-1.0]])],"derivedFrom":subQ1}),-1.0]])]});}
            var Q44;
            {var subQ0=sQuery(id+"F2.wireOp",EDGE,"E26.bottom");var subQ1=sQuery(id+"F2.wireOp",EDGE,"E22");var subQ2=makeQuery(id+"F2.imprint","INTERSECT",VERTEX,{"derivedFrom":[subQ1,subQ0]});Q44=makeQuery(id+"F2.imprint","IMPRINT",FACE,{"disambiguationData":[TD([[makeQuery(id+"F2.imprint","IMPRINT",EDGE,{"disambiguationData":[TD([[subQ2,-1.0]])],"derivedFrom":subQ1}),-1.0]])]});}
            var Q45;
            {var subQ0=sQuery(id+"F2.wireOp",EDGE,"E29");var subQ1=sQuery(id+"F2.wireOp",EDGE,"E16");var subQ2=makeQuery(id+"F2.imprint","INTERSECT",VERTEX,{"derivedFrom":[subQ1,subQ0]});Q45=makeQuery(id+"F2.imprint","IMPRINT",FACE,{"disambiguationData":[TD([[makeQuery(id+"F2.imprint","IMPRINT",EDGE,{"disambiguationData":[TD([[subQ2,-1.0]])],"derivedFrom":subQ1}),-1.0]])]});}
            var Q46;
            {var subQ0=sQuery(id+"F2.wireOp",EDGE,"E27");var subQ1=sQuery(id+"F2.wireOp",EDGE,"E16");var subQ2=makeQuery(id+"F2.imprint","INTERSECT",VERTEX,{"derivedFrom":[subQ1,subQ0]});Q46=makeQuery(id+"F2.imprint","IMPRINT",FACE,{"disambiguationData":[TD([[makeQuery(id+"F2.imprint","IMPRINT",EDGE,{"disambiguationData":[TD([[subQ2,-1.0]])],"derivedFrom":subQ1}),-1.0]])]});}
            var Q47;
            {var subQ0=sQuery(id+"F2.wireOp",EDGE,"E31");var subQ1=sQuery(id+"F2.wireOp",EDGE,"E16");var subQ2=makeQuery(id+"F2.imprint","INTERSECT",VERTEX,{"derivedFrom":[subQ1,subQ0]});Q47=makeQuery(id+"F2.imprint","IMPRINT",FACE,{"disambiguationData":[TD([[makeQuery(id+"F2.imprint","IMPRINT",EDGE,{"disambiguationData":[TD([[subQ2,-1.0]])],"derivedFrom":subQ1}),-1.0]])]});}
            var Q48;
            {var subQ0=sQuery(id+"F2.wireOp",EDGE,"E29");var subQ1=sQuery(id+"F2.wireOp",EDGE,"E16");var subQ2=makeQuery(id+"F2.imprint","INTERSECT",VERTEX,{"derivedFrom":[subQ1,subQ0]});Q48=makeQuery(id+"F2.imprint","IMPRINT",FACE,{"disambiguationData":[TD([[makeQuery(id+"F2.imprint","IMPRINT",EDGE,{"disambiguationData":[TD([[subQ2,1.0]])],"derivedFrom":subQ1}),-1.0]])]});}
            extrude(context, id + "F3", {"entities" : qUnion([Q0, Q1, Q2, Q3, Q4, Q5, Q6, Q7, Q8, Q9, Q10, Q11, Q12, Q13, Q14, Q15, Q16, Q17, Q18, Q19, Q20, Q21, Q22, Q23, Q24, Q25, Q26, Q27, Q28, Q29, Q30, Q31, Q32, Q33, Q34, Q35, Q36, Q37, Q38, Q39, Q40, Q41, Q42, Q43, Q44, Q45, Q46, Q47, Q48]), "operationType" : NewBodyOperationType.ADD, "depth" : 25.4 * mm});
        }
        {
            var Q0;
            Q0=makeQuery(id+"F3.boolean.opBoolean","MERGE",FACE,{"derivedFrom":[makeQuery(id+"F1.opExtrude","CAP_FACE",FACE,{"disambiguationData":[OSD([sQuery(id+"F0.wireOp",EDGE,"E1"),sQuery(id+"F0.wireOp",EDGE,"E9.bottom"),sQuery(id+"F0.wireOp",EDGE,"E9.top"),sQuery(id+"F0.wireOp",EDGE,"E9.left"),sQuery(id+"F0.wireOp",EDGE,"E9.right"),sQuery(id+"F0.wireOp",EDGE,"E10"),sQuery(id+"F0.wireOp",EDGE,"E11"),sQuery(id+"F0.wireOp",EDGE,"E12"),sQuery(id+"F0.wireOp",EDGE,"E13")])],"isStart":false}),makeQuery(id+"F3.opExtrude","CAP_FACE",FACE,{"disambiguationData":[OSD([sQuery(id+"F2.wireOp",EDGE,"E17"),sQuery(id+"F2.wireOp",EDGE,"E22"),sQuery(id+"F2.wireOp",EDGE,"E23"),sQuery(id+"F2.wireOp",EDGE,"E24"),sQuery(id+"F2.wireOp",EDGE,"E25"),sQuery(id+"F2.wireOp",EDGE,"E26.bottom"),sQuery(id+"F2.wireOp",EDGE,"E26.top"),sQuery(id+"F2.wireOp",EDGE,"E26.left"),sQuery(id+"F2.wireOp",EDGE,"E26.right"),sQuery(id+"F2.wireOp",EDGE,"E27"),sQuery(id+"F2.wireOp",EDGE,"E28"),sQuery(id+"F2.wireOp",EDGE,"E29"),sQuery(id+"F2.wireOp",EDGE,"E30"),sQuery(id+"F2.wireOp",EDGE,"E31"),sQuery(id+"F2.wireOp",EDGE,"E32"),sQuery(id+"F2.wireOp",EDGE,"E33"),sQuery(id+"F2.wireOp",EDGE,"E34")])],"isStart":false})]});
            var sketch = newSketch(context, id + "F4", { "sketchPlane" : qUnion([Q0])});
            skCircle(sketch, "E35", {"center": v(0, 0) * mm, "radius": 6.35 * mm});
            skSolve(sketch);
        }
        {
            var Q0;
            Q0=makeQuery(id+"F4.imprint","IMPRINT",FACE,{"disambiguationData":[TD([[makeQuery(id+"F4.imprint","IMPRINT",EDGE,{"derivedFrom":sQuery(id+"F4.wireOp",EDGE,"gMkGZPPQ-I52G-XJL4-xDoI-vPj4hhmsiVuW")}),1.0]])]});
            var Q1;
            Q1=makeQuery(id+"F4.imprint","IMPRINT",FACE,{"disambiguationData":[TD([[makeQuery(id+"F4.imprint","IMPRINT",EDGE,{"derivedFrom":sQuery(id+"F4.wireOp",EDGE,"E35")}),1.0]])]});
            extrude(context, id + "F5", {"entities" : qUnion([Q0, Q1]), "operationType" : NewBodyOperationType.REMOVE, "oppositeDirection" : true, "depth" : 25.4 * mm});
        }
        {
            var Q0;
            Q0=makeQuery(id+"F1.opExtrude","SWEPT_EDGE",EDGE,{"disambiguationData":[OSD([sQuery(id+"F0.wireOp",EDGE,"E9.top"),sQuery(id+"F0.wireOp",EDGE,"E9.left")])]});
            var Q1;
            Q1=makeQuery(id+"F1.opExtrude","SWEPT_EDGE",EDGE,{"disambiguationData":[OSD([sQuery(id+"F0.wireOp",EDGE,"E9.top"),sQuery(id+"F0.wireOp",EDGE,"E9.right")])]});
            var Q2;
            Q2=makeQuery(id+"F1.opExtrude","SWEPT_EDGE",EDGE,{"disambiguationData":[OSD([sQuery(id+"F0.wireOp",EDGE,"E10"),sQuery(id+"F0.wireOp",EDGE,"E12")])]});
            var Q3;
            Q3=makeQuery(id+"F1.opExtrude","SWEPT_EDGE",EDGE,{"disambiguationData":[OSD([sQuery(id+"F0.wireOp",EDGE,"E11"),sQuery(id+"F0.wireOp",EDGE,"E12")])]});
            var Q4;
            Q4=makeQuery(id+"F3.opExtrude","SWEPT_EDGE",EDGE,{"disambiguationData":[OSD([sQuery(id+"F2.wireOp",EDGE,"E22"),sQuery(id+"F2.wireOp",EDGE,"E23")])]});
            var Q5;
            Q5=makeQuery(id+"F3.opExtrude","SWEPT_EDGE",EDGE,{"disambiguationData":[OSD([sQuery(id+"F2.wireOp",EDGE,"E23"),sQuery(id+"F2.wireOp",EDGE,"E24")])]});
            var Q6;
            Q6=makeQuery(id+"F3.opExtrude","SWEPT_EDGE",EDGE,{"disambiguationData":[OSD([sQuery(id+"F2.wireOp",EDGE,"E33"),sQuery(id+"F2.wireOp",EDGE,"E34")])]});
            var Q7;
            Q7=makeQuery(id+"F3.opExtrude","SWEPT_EDGE",EDGE,{"disambiguationData":[OSD([sQuery(id+"F2.wireOp",EDGE,"E31"),sQuery(id+"F2.wireOp",EDGE,"E34")])]});
            var Q8;
            Q8=makeQuery(id+"F3.opExtrude","SWEPT_EDGE",EDGE,{"disambiguationData":[OSD([sQuery(id+"F2.wireOp",EDGE,"E29"),sQuery(id+"F2.wireOp",EDGE,"E30")])]});
            var Q9;
            Q9=makeQuery(id+"F3.opExtrude","SWEPT_EDGE",EDGE,{"disambiguationData":[OSD([sQuery(id+"F2.wireOp",EDGE,"E27"),sQuery(id+"F2.wireOp",EDGE,"E30")])]});
            var Q10;
            Q10=makeQuery(id+"F3.opExtrude","SWEPT_EDGE",EDGE,{"disambiguationData":[OSD([sQuery(id+"F2.wireOp",EDGE,"E26.bottom"),sQuery(id+"F2.wireOp",EDGE,"E26.left")])]});
            var Q11;
            Q11=makeQuery(id+"F3.opExtrude","SWEPT_EDGE",EDGE,{"disambiguationData":[OSD([sQuery(id+"F2.wireOp",EDGE,"E26.top"),sQuery(id+"F2.wireOp",EDGE,"E26.left")])]});
            var Q12;
            Q12=makeQuery(id+"F3.opExtrude","SWEPT_EDGE",EDGE,{"disambiguationData":[OSD([sQuery(id+"F2.wireOp",EDGE,"E24"),sQuery(id+"F2.wireOp",EDGE,"E25")])]});
            var Q13;
            Q13=makeQuery(id+"F3.opExtrude","SWEPT_EDGE",EDGE,{"disambiguationData":[OSD([sQuery(id+"F2.wireOp",EDGE,"E22"),sQuery(id+"F2.wireOp",EDGE,"E25")])]});
            var Q14;
            Q14=makeQuery(id+"F1.opExtrude","SWEPT_EDGE",EDGE,{"disambiguationData":[OSD([sQuery(id+"F0.wireOp",EDGE,"E10"),sQuery(id+"F0.wireOp",EDGE,"E13")])]});
            var Q15;
            Q15=makeQuery(id+"F1.opExtrude","SWEPT_EDGE",EDGE,{"disambiguationData":[OSD([sQuery(id+"F0.wireOp",EDGE,"E11"),sQuery(id+"F0.wireOp",EDGE,"E13")])]});
            var Q16;
            Q16=makeQuery(id+"F1.opExtrude","SWEPT_EDGE",EDGE,{"disambiguationData":[OSD([sQuery(id+"F0.wireOp",EDGE,"E9.bottom"),sQuery(id+"F0.wireOp",EDGE,"E9.left")])]});
            var Q17;
            Q17=makeQuery(id+"F1.opExtrude","SWEPT_EDGE",EDGE,{"disambiguationData":[OSD([sQuery(id+"F0.wireOp",EDGE,"E9.bottom"),sQuery(id+"F0.wireOp",EDGE,"E9.right")])]});
            var Q18;
            Q18=makeQuery(id+"F3.opExtrude","SWEPT_EDGE",EDGE,{"disambiguationData":[OSD([sQuery(id+"F2.wireOp",EDGE,"E31"),sQuery(id+"F2.wireOp",EDGE,"E32")])]});
            var Q19;
            Q19=makeQuery(id+"F3.opExtrude","SWEPT_EDGE",EDGE,{"disambiguationData":[OSD([sQuery(id+"F2.wireOp",EDGE,"E32"),sQuery(id+"F2.wireOp",EDGE,"E33")])]});
            var Q20;
            Q20=makeQuery(id+"F3.opExtrude","SWEPT_EDGE",EDGE,{"disambiguationData":[OSD([sQuery(id+"F2.wireOp",EDGE,"E27"),sQuery(id+"F2.wireOp",EDGE,"E28")])]});
            var Q21;
            Q21=makeQuery(id+"F3.opExtrude","SWEPT_EDGE",EDGE,{"disambiguationData":[OSD([sQuery(id+"F2.wireOp",EDGE,"E28"),sQuery(id+"F2.wireOp",EDGE,"E29")])]});
            var Q22;
            Q22=makeQuery(id+"F3.opExtrude","SWEPT_EDGE",EDGE,{"disambiguationData":[OSD([sQuery(id+"F2.wireOp",EDGE,"E26.top"),sQuery(id+"F2.wireOp",EDGE,"E26.right")])]});
            var Q23;
            Q23=makeQuery(id+"F3.opExtrude","SWEPT_EDGE",EDGE,{"disambiguationData":[OSD([sQuery(id+"F2.wireOp",EDGE,"E26.bottom"),sQuery(id+"F2.wireOp",EDGE,"E26.right")])]});
            fillet(context, id + "F6", {"entities" : qUnion([Q0, Q1, Q2, Q3, Q4, Q5, Q6, Q7, Q8, Q9, Q10, Q11, Q12, Q13, Q14, Q15, Q16, Q17, Q18, Q19, Q20, Q21, Q22, Q23]), "radius" : 8.9 * mm, "tangentPropagation" : true, "allowEdgeOverflow" : false});
        }
        {
            var Q0;
            {var subQ0=sQuery(id+"F2.wireOp",EDGE,"E33");var subQ1=sQuery(id+"F2.wireOp",EDGE,"E17");Q0=makeQuery(id+"F3.opExtrude","SWEPT_EDGE",EDGE,{"disambiguationData":[OSD([subQ1,subQ0]),TDD([makeQuery(id+"F2.imprint","INTERSECT",VERTEX,{"disambiguationData":[OD(0.0)],"derivedFrom":[subQ1,subQ0]})])]});}
            var Q1;
            {var subQ0=sQuery(id+"F0.wireOp",EDGE,"E9.left");var subQ1=sQuery(id+"F0.wireOp",EDGE,"E1");Q1=makeQuery(id+"F1.opExtrude","SWEPT_EDGE",EDGE,{"disambiguationData":[OSD([subQ1,subQ0]),TDD([makeQuery(id+"F0.imprint","INTERSECT",VERTEX,{"disambiguationData":[OD(0.0)],"derivedFrom":[subQ1,subQ0]})])]});}
            var Q2;
            {var subQ0=sQuery(id+"F2.wireOp",EDGE,"E29");var subQ1=sQuery(id+"F2.wireOp",EDGE,"E17");Q2=makeQuery(id+"F3.opExtrude","SWEPT_EDGE",EDGE,{"disambiguationData":[OSD([subQ1,subQ0]),TDD([makeQuery(id+"F2.imprint","INTERSECT",VERTEX,{"disambiguationData":[OD(0.0)],"derivedFrom":[subQ1,subQ0]})])]});}
            var Q3;
            {var subQ0=sQuery(id+"F2.wireOp",EDGE,"E31");var subQ1=sQuery(id+"F2.wireOp",EDGE,"E17");Q3=makeQuery(id+"F3.opExtrude","SWEPT_EDGE",EDGE,{"disambiguationData":[OSD([subQ1,subQ0]),TDD([makeQuery(id+"F2.imprint","INTERSECT",VERTEX,{"disambiguationData":[OD(0.0)],"derivedFrom":[subQ1,subQ0]})])]});}
            var Q4;
            {var subQ0=sQuery(id+"F2.wireOp",EDGE,"E26.bottom");var subQ1=sQuery(id+"F2.wireOp",EDGE,"E17");Q4=makeQuery(id+"F3.opExtrude","SWEPT_EDGE",EDGE,{"disambiguationData":[OSD([subQ1,subQ0]),TDD([makeQuery(id+"F2.imprint","INTERSECT",VERTEX,{"disambiguationData":[OD(1.0)],"derivedFrom":[subQ1,subQ0]})])]});}
            var Q5;
            {var subQ0=sQuery(id+"F2.wireOp",EDGE,"E27");var subQ1=sQuery(id+"F2.wireOp",EDGE,"E17");Q5=makeQuery(id+"F3.opExtrude","SWEPT_EDGE",EDGE,{"disambiguationData":[OSD([subQ1,subQ0]),TDD([makeQuery(id+"F2.imprint","INTERSECT",VERTEX,{"disambiguationData":[OD(0.0)],"derivedFrom":[subQ1,subQ0]})])]});}
            var Q6;
            {var subQ0=sQuery(id+"F2.wireOp",EDGE,"E22");var subQ1=sQuery(id+"F2.wireOp",EDGE,"E17");Q6=makeQuery(id+"F3.opExtrude","SWEPT_EDGE",EDGE,{"disambiguationData":[OSD([subQ1,subQ0]),TDD([makeQuery(id+"F2.imprint","INTERSECT",VERTEX,{"disambiguationData":[OD(1.0)],"derivedFrom":[subQ1,subQ0]})])]});}
            var Q7;
            {var subQ0=sQuery(id+"F2.wireOp",EDGE,"E26.top");var subQ1=sQuery(id+"F2.wireOp",EDGE,"E17");Q7=makeQuery(id+"F3.opExtrude","SWEPT_EDGE",EDGE,{"disambiguationData":[OSD([subQ1,subQ0]),TDD([makeQuery(id+"F2.imprint","INTERSECT",VERTEX,{"disambiguationData":[OD(0.0)],"derivedFrom":[subQ1,subQ0]})])]});}
            var Q8;
            {var subQ0=sQuery(id+"F2.wireOp",EDGE,"E24");var subQ1=sQuery(id+"F2.wireOp",EDGE,"E17");Q8=makeQuery(id+"F3.opExtrude","SWEPT_EDGE",EDGE,{"disambiguationData":[OSD([subQ1,subQ0]),TDD([makeQuery(id+"F2.imprint","INTERSECT",VERTEX,{"disambiguationData":[OD(1.0)],"derivedFrom":[subQ1,subQ0]})])]});}
            var Q9;
            {var subQ0=sQuery(id+"F0.wireOp",EDGE,"E10");var subQ1=sQuery(id+"F0.wireOp",EDGE,"E1");Q9=makeQuery(id+"F1.opExtrude","SWEPT_EDGE",EDGE,{"disambiguationData":[OSD([subQ1,subQ0]),TDD([makeQuery(id+"F0.imprint","INTERSECT",VERTEX,{"disambiguationData":[OD(1.0)],"derivedFrom":[subQ1,subQ0]})])]});}
            var Q10;
            {var subQ0=sQuery(id+"F0.wireOp",EDGE,"E11");var subQ1=sQuery(id+"F0.wireOp",EDGE,"E1");Q10=makeQuery(id+"F1.opExtrude","SWEPT_EDGE",EDGE,{"disambiguationData":[OSD([subQ1,subQ0]),TDD([makeQuery(id+"F0.imprint","INTERSECT",VERTEX,{"disambiguationData":[OD(1.0)],"derivedFrom":[subQ1,subQ0]})])]});}
            var Q11;
            {var subQ0=sQuery(id+"F0.wireOp",EDGE,"E9.left");var subQ1=sQuery(id+"F0.wireOp",EDGE,"E1");Q11=makeQuery(id+"F1.opExtrude","SWEPT_EDGE",EDGE,{"disambiguationData":[OSD([subQ1,subQ0]),TDD([makeQuery(id+"F0.imprint","INTERSECT",VERTEX,{"disambiguationData":[OD(1.0)],"derivedFrom":[subQ1,subQ0]})])]});}
            var Q12;
            {var subQ0=sQuery(id+"F0.wireOp",EDGE,"E9.right");var subQ1=sQuery(id+"F0.wireOp",EDGE,"E1");Q12=makeQuery(id+"F1.opExtrude","SWEPT_EDGE",EDGE,{"disambiguationData":[OSD([subQ1,subQ0]),TDD([makeQuery(id+"F0.imprint","INTERSECT",VERTEX,{"disambiguationData":[OD(1.0)],"derivedFrom":[subQ1,subQ0]})])]});}
            var Q13;
            {var subQ0=sQuery(id+"F2.wireOp",EDGE,"E31");var subQ1=sQuery(id+"F2.wireOp",EDGE,"E17");Q13=makeQuery(id+"F3.opExtrude","SWEPT_EDGE",EDGE,{"disambiguationData":[OSD([subQ1,subQ0]),TDD([makeQuery(id+"F2.imprint","INTERSECT",VERTEX,{"disambiguationData":[OD(1.0)],"derivedFrom":[subQ1,subQ0]})])]});}
            var Q14;
            {var subQ0=sQuery(id+"F2.wireOp",EDGE,"E27");var subQ1=sQuery(id+"F2.wireOp",EDGE,"E17");Q14=makeQuery(id+"F3.opExtrude","SWEPT_EDGE",EDGE,{"disambiguationData":[OSD([subQ1,subQ0]),TDD([makeQuery(id+"F2.imprint","INTERSECT",VERTEX,{"disambiguationData":[OD(1.0)],"derivedFrom":[subQ1,subQ0]})])]});}
            var Q15;
            {var subQ0=sQuery(id+"F2.wireOp",EDGE,"E33");var subQ1=sQuery(id+"F2.wireOp",EDGE,"E17");Q15=makeQuery(id+"F3.opExtrude","SWEPT_EDGE",EDGE,{"disambiguationData":[OSD([subQ1,subQ0]),TDD([makeQuery(id+"F2.imprint","INTERSECT",VERTEX,{"disambiguationData":[OD(1.0)],"derivedFrom":[subQ1,subQ0]})])]});}
            var Q16;
            {var subQ0=sQuery(id+"F2.wireOp",EDGE,"E26.top");var subQ1=sQuery(id+"F2.wireOp",EDGE,"E17");Q16=makeQuery(id+"F3.opExtrude","SWEPT_EDGE",EDGE,{"disambiguationData":[OSD([subQ1,subQ0]),TDD([makeQuery(id+"F2.imprint","INTERSECT",VERTEX,{"disambiguationData":[OD(1.0)],"derivedFrom":[subQ1,subQ0]})])]});}
            var Q17;
            {var subQ0=sQuery(id+"F2.wireOp",EDGE,"E29");var subQ1=sQuery(id+"F2.wireOp",EDGE,"E17");Q17=makeQuery(id+"F3.opExtrude","SWEPT_EDGE",EDGE,{"disambiguationData":[OSD([subQ1,subQ0]),TDD([makeQuery(id+"F2.imprint","INTERSECT",VERTEX,{"disambiguationData":[OD(1.0)],"derivedFrom":[subQ1,subQ0]})])]});}
            var Q18;
            {var subQ0=sQuery(id+"F2.wireOp",EDGE,"E26.bottom");var subQ1=sQuery(id+"F2.wireOp",EDGE,"E17");Q18=makeQuery(id+"F3.opExtrude","SWEPT_EDGE",EDGE,{"disambiguationData":[OSD([subQ1,subQ0]),TDD([makeQuery(id+"F2.imprint","INTERSECT",VERTEX,{"disambiguationData":[OD(0.0)],"derivedFrom":[subQ1,subQ0]})])]});}
            var Q19;
            {var subQ0=sQuery(id+"F2.wireOp",EDGE,"E24");var subQ1=sQuery(id+"F2.wireOp",EDGE,"E17");Q19=makeQuery(id+"F3.opExtrude","SWEPT_EDGE",EDGE,{"disambiguationData":[OSD([subQ1,subQ0]),TDD([makeQuery(id+"F2.imprint","INTERSECT",VERTEX,{"disambiguationData":[OD(0.0)],"derivedFrom":[subQ1,subQ0]})])]});}
            var Q20;
            {var subQ0=sQuery(id+"F2.wireOp",EDGE,"E22");var subQ1=sQuery(id+"F2.wireOp",EDGE,"E17");Q20=makeQuery(id+"F3.opExtrude","SWEPT_EDGE",EDGE,{"disambiguationData":[OSD([subQ1,subQ0]),TDD([makeQuery(id+"F2.imprint","INTERSECT",VERTEX,{"disambiguationData":[OD(0.0)],"derivedFrom":[subQ1,subQ0]})])]});}
            var Q21;
            {var subQ0=sQuery(id+"F0.wireOp",EDGE,"E11");var subQ1=sQuery(id+"F0.wireOp",EDGE,"E1");Q21=makeQuery(id+"F1.opExtrude","SWEPT_EDGE",EDGE,{"disambiguationData":[OSD([subQ1,subQ0]),TDD([makeQuery(id+"F0.imprint","INTERSECT",VERTEX,{"disambiguationData":[OD(0.0)],"derivedFrom":[subQ1,subQ0]})])]});}
            var Q22;
            {var subQ0=sQuery(id+"F0.wireOp",EDGE,"E9.right");var subQ1=sQuery(id+"F0.wireOp",EDGE,"E1");Q22=makeQuery(id+"F1.opExtrude","SWEPT_EDGE",EDGE,{"disambiguationData":[OSD([subQ1,subQ0]),TDD([makeQuery(id+"F0.imprint","INTERSECT",VERTEX,{"disambiguationData":[OD(0.0)],"derivedFrom":[subQ1,subQ0]})])]});}
            var Q23;
            {var subQ0=sQuery(id+"F0.wireOp",EDGE,"E10");var subQ1=sQuery(id+"F0.wireOp",EDGE,"E1");Q23=makeQuery(id+"F1.opExtrude","SWEPT_EDGE",EDGE,{"disambiguationData":[OSD([subQ1,subQ0]),TDD([makeQuery(id+"F0.imprint","INTERSECT",VERTEX,{"disambiguationData":[OD(0.0)],"derivedFrom":[subQ1,subQ0]})])]});}
            fillet(context, id + "F7", {"entities" : qUnion([Q0, Q1, Q2, Q3, Q4, Q5, Q6, Q7, Q8, Q9, Q10, Q11, Q12, Q13, Q14, Q15, Q16, Q17, Q18, Q19, Q20, Q21, Q22, Q23]), "radius" : 5.08 * mm, "tangentPropagation" : true, "allowEdgeOverflow" : false});
        }
    });
